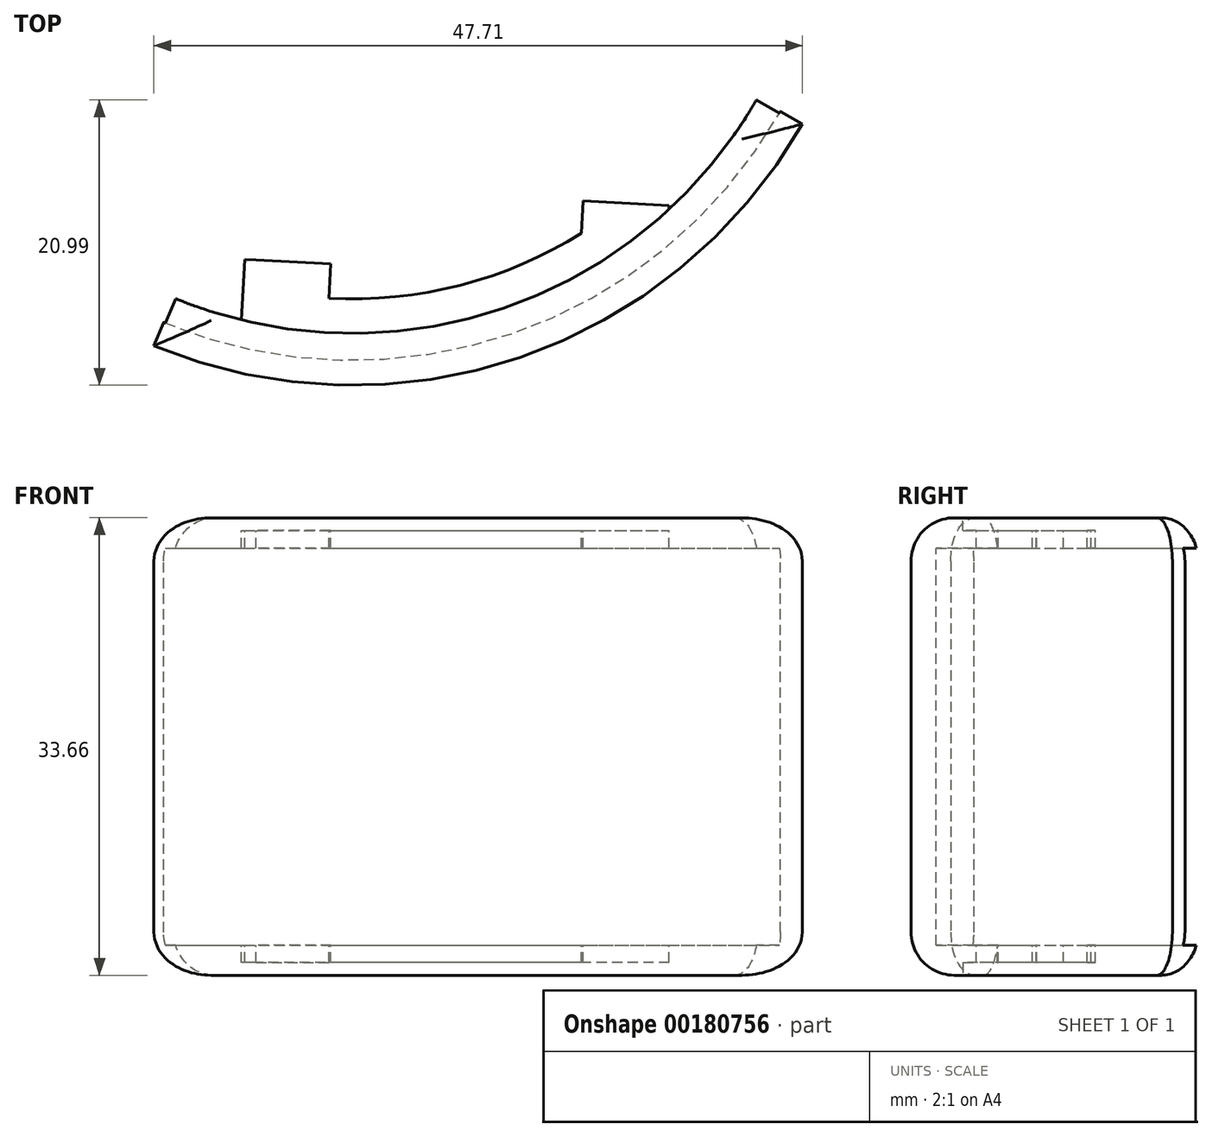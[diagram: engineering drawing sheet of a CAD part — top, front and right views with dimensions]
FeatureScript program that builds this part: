
annotation { "Feature Type Name" : "Feature", "Feature Type Description" : "" }
export const myFeature = defineFeature(function(context is Context, id is Id, definition is map)
    precondition{}
    {
        {
            var Q0;
            Q0=qCreatedBy(makeId("Top.planeOp"),FACE);
            var sketch = newSketch(context, id + "F0", { "sketchPlane" : qUnion([Q0])});
            skCircle(sketch, "E0", {"center": v(-38.1, 38.1) * mm, "radius": 38.1 * mm});
            skCircle(sketch, "E1", {"center": v(-38.1, 38.1) * mm, "radius": 35.3 * mm});
            skLineSegment(sketch, "E2", {"start": v(-5, 19.23) * mm, "end": v(-38.1, 38.1) * mm});
            skLineSegment(sketch, "E3", {"start": v(-38.1, 38.1) * mm, "end": v(-52.7, 2.91) * mm});
            skCircle(sketch, "E4", {"center": v(-38.1, 38.1) * mm, "radius": 28.96 * mm});
            skSolve(sketch);
        }
        {
            var Q0;
            {var subQ0=sQuery(id+"F0.wireOp",EDGE,"E2");var subQ1=sQuery(id+"F0.wireOp",EDGE,"E0");var subQ2=makeQuery(id+"F0.imprint","INTERSECT",VERTEX,{"derivedFrom":[subQ1,subQ0]});Q0=makeQuery(id+"F0.imprint","IMPRINT",FACE,{"disambiguationData":[TD([[makeQuery(id+"F0.imprint","IMPRINT",EDGE,{"disambiguationData":[TD([[subQ2,1.0]])],"derivedFrom":subQ1}),1.0]])]});}
            var Q1;
            {var subQ0=sQuery(id+"F0.wireOp",EDGE,"E2");var subQ1=sQuery(id+"F0.wireOp",EDGE,"E1");var subQ2=makeQuery(id+"F0.imprint","INTERSECT",VERTEX,{"derivedFrom":[subQ1,subQ0]});Q1=makeQuery(id+"F0.imprint","IMPRINT",FACE,{"disambiguationData":[TD([[makeQuery(id+"F0.imprint","IMPRINT",EDGE,{"disambiguationData":[TD([[subQ2,1.0]])],"derivedFrom":subQ1}),1.0]])]});}
            extrude(context, id + "F1", {"entities" : qUnion([Q0, Q1]), "endBound" : BoundingType.SYMMETRIC, "depth" : 33.65 * mm});
        }
        {
            var Q0;
            Q0=makeQuery(id+"F1.opExtrude","CAP_FACE",FACE,{"disambiguationData":[OSD([sQuery(id+"F0.wireOp",EDGE,"E0"),sQuery(id+"F0.wireOp",EDGE,"E2"),sQuery(id+"F0.wireOp",EDGE,"E3"),sQuery(id+"F0.wireOp",EDGE,"E4")])],"isStart":false});
            var sketch = newSketch(context, id + "F2", { "sketchPlane" : qUnion([Q0])});
            skCircle(sketch, "E5", {"center": v(-38.1, 38.1) * mm, "radius": 34.3 * mm});
            skSolve(sketch);
        }
        {
            var Q0;
            Q0 = qSketchRegion(id + "F2", true);
            extrude(context, id + "F3", {"entities" : qUnion([Q0]), "operationType" : NewBodyOperationType.REMOVE, "oppositeDirection" : true, "depth" : 0.94 * mm});
        }
        {
            var Q0;
            Q0=makeQuery(id+"F1.opExtrude","CAP_FACE",FACE,{"disambiguationData":[OSD([sQuery(id+"F0.wireOp",EDGE,"E0"),sQuery(id+"F0.wireOp",EDGE,"E2"),sQuery(id+"F0.wireOp",EDGE,"E3"),sQuery(id+"F0.wireOp",EDGE,"E4")])],"isStart":true});
            var sketch = newSketch(context, id + "F4", { "sketchPlane" : qUnion([Q0])});
            skCircle(sketch, "E6", {"center": v(-38.1, -38.1) * mm, "radius": 34.3 * mm});
            skSolve(sketch);
        }
        {
            var Q0;
            Q0 = qSketchRegion(id + "F4", true);
            extrude(context, id + "F5", {"entities" : qUnion([Q0]), "operationType" : NewBodyOperationType.REMOVE, "oppositeDirection" : true, "depth" : 0.94 * mm});
        }
        {
            var Q0;
            Q0=qCreatedBy(makeId("Top.planeOp"),FACE);
            var sketch = newSketch(context, id + "F6", { "sketchPlane" : qUnion([Q0])});
            skCircle(sketch, "E7", {"center": v(-38.1, 38.1) * mm, "radius": 36.25 * mm});
            skSolve(sketch);
        }
        {
            var Q0;
            Q0 = qSketchRegion(id + "F6", true);
            extrude(context, id + "F7", {"entities" : qUnion([Q0]), "operationType" : NewBodyOperationType.REMOVE, "endBound" : BoundingType.SYMMETRIC, "oppositeDirection" : true, "depth" : 29.2 * mm});
        }
        {
            var Q0;
            Q0=makeQuery(id+"F1.opExtrude","CAP_EDGE",EDGE,{"disambiguationData":[OSD([sQuery(id+"F0.wireOp",EDGE,"E2")])],"isStart":false});
            var Q1;
            Q1=makeQuery(id+"F1.opExtrude","CAP_EDGE",EDGE,{"disambiguationData":[OSD([sQuery(id+"F0.wireOp",EDGE,"E2")])],"isStart":true});
            var Q2;
            Q2=makeQuery(id+"F1.opExtrude","CAP_EDGE",EDGE,{"disambiguationData":[OSD([sQuery(id+"F0.wireOp",EDGE,"E3")])],"isStart":false});
            var Q3;
            Q3=makeQuery(id+"F1.opExtrude","CAP_EDGE",EDGE,{"disambiguationData":[OSD([sQuery(id+"F0.wireOp",EDGE,"E3")])],"isStart":true});
            fillet(context, id + "F8", {"entities" : qUnion([Q0, Q1, Q2, Q3]), "radius" : 3.17 * mm, "tangentPropagation" : true, "allowEdgeOverflow" : false});
        }
        {
            var Q0;
            Q0=makeQuery(id+"F1.opExtrude","CAP_EDGE",EDGE,{"disambiguationData":[OSD([sQuery(id+"F0.wireOp",EDGE,"E0")])],"isStart":false});
            var Q1;
            Q1=makeQuery(id+"F1.opExtrude","CAP_EDGE",EDGE,{"disambiguationData":[OSD([sQuery(id+"F0.wireOp",EDGE,"E0")])],"isStart":true});
            fillet(context, id + "F9", {"entities" : qUnion([Q0, Q1]), "radius" : 3.17 * mm, "allowEdgeOverflow" : false});
        }
        {
            var Q0;
            Q0=qCreatedBy(makeId("Top.planeOp"),FACE);
            var sketch = newSketch(context, id + "F10", { "sketchPlane" : qUnion([Q0])});
            skCircle(sketch, "E8", {"center": v(-38.1, 38.1) * mm, "radius": 34.3 * mm});
            skLineSegment(sketch, "E9", {"start": v(-46.27, 4.8) * mm, "end": v(-38.1, 38.1) * mm});
            skLineSegment(sketch, "E10", {"start": v(-38.1, 38.1) * mm, "end": v(-14.8, 12.95) * mm});
            skCircle(sketch, "E11", {"center": v(-38.1, 38.1) * mm, "radius": 31.75 * mm});
            skLineSegment(sketch, "E12", {"start": v(-39.83, 6.4) * mm, "end": v(-39.7, 8.93) * mm});
            skLineSegment(sketch, "E13", {"start": v(-39.7, 8.93) * mm, "end": v(-45.18, 9.22) * mm});
            skLineSegment(sketch, "E14", {"start": v(-21.25, 11.2) * mm, "end": v(-21.12, 13.56) * mm});
            skLineSegment(sketch, "E15", {"start": v(-21.12, 13.56) * mm, "end": v(-15.07, 13.24) * mm});
            skLineSegment(sketch, "E16", {"start": v(-15.07, 13.24) * mm, "end": v(-14.8, 13.22) * mm});
            skLineSegment(sketch, "E17", {"start": v(-14.8, 13.22) * mm, "end": v(-14.8, 12.95) * mm});
            skLineSegment(sketch, "E18", {"start": v(-46.27, 4.8) * mm, "end": v(-46.04, 9.24) * mm});
            skLineSegment(sketch, "E19", {"start": v(-46.04, 9.24) * mm, "end": v(-45.18, 9.22) * mm});
            skSolve(sketch);
        }
        {
            var Q0;
            {var subQ0=sQuery(id+"F10.wireOp",EDGE,"E16");Q0=makeQuery(id+"F10.imprint","IMPRINT",FACE,{"disambiguationData":[TD([[makeQuery(id+"F10.imprint","IMPRINT",EDGE,{"derivedFrom":subQ0}),1.0]])]});}
            var Q1;
            {var subQ0=sQuery(id+"F10.wireOp",EDGE,"E19");Q1=makeQuery(id+"F10.imprint","IMPRINT",FACE,{"disambiguationData":[TD([[makeQuery(id+"F10.imprint","IMPRINT",EDGE,{"derivedFrom":subQ0}),1.0]])]});}
            var Q2;
            {var subQ0=sQuery(id+"F10.wireOp",EDGE,"E12");Q2=makeQuery(id+"F10.imprint","IMPRINT",FACE,{"disambiguationData":[TD([[makeQuery(id+"F10.imprint","IMPRINT",EDGE,{"derivedFrom":subQ0}),-1.0]])]});}
            var Q3;
            {var subQ1=sQuery(id+"F10.wireOp",EDGE,"E10");var subQ3=sQuery(id+"F10.wireOp",EDGE,"E11");var subQ4=makeQuery(id+"F10.imprint","INTERSECT",VERTEX,{"derivedFrom":[subQ1,subQ3]});Q3=makeQuery(id+"F10.imprint","IMPRINT",FACE,{"disambiguationData":[TD([[makeQuery(id+"F10.imprint","IMPRINT",EDGE,{"disambiguationData":[TD([[subQ4,1.0]])],"derivedFrom":subQ3}),-1.0]])]});}
            extrude(context, id + "F11", {"entities" : qUnion([Q0, Q1, Q2, Q3]), "operationType" : NewBodyOperationType.REMOVE, "endBound" : BoundingType.SYMMETRIC, "oppositeDirection" : true, "depth" : 32.5 * mm});
        }
    });
